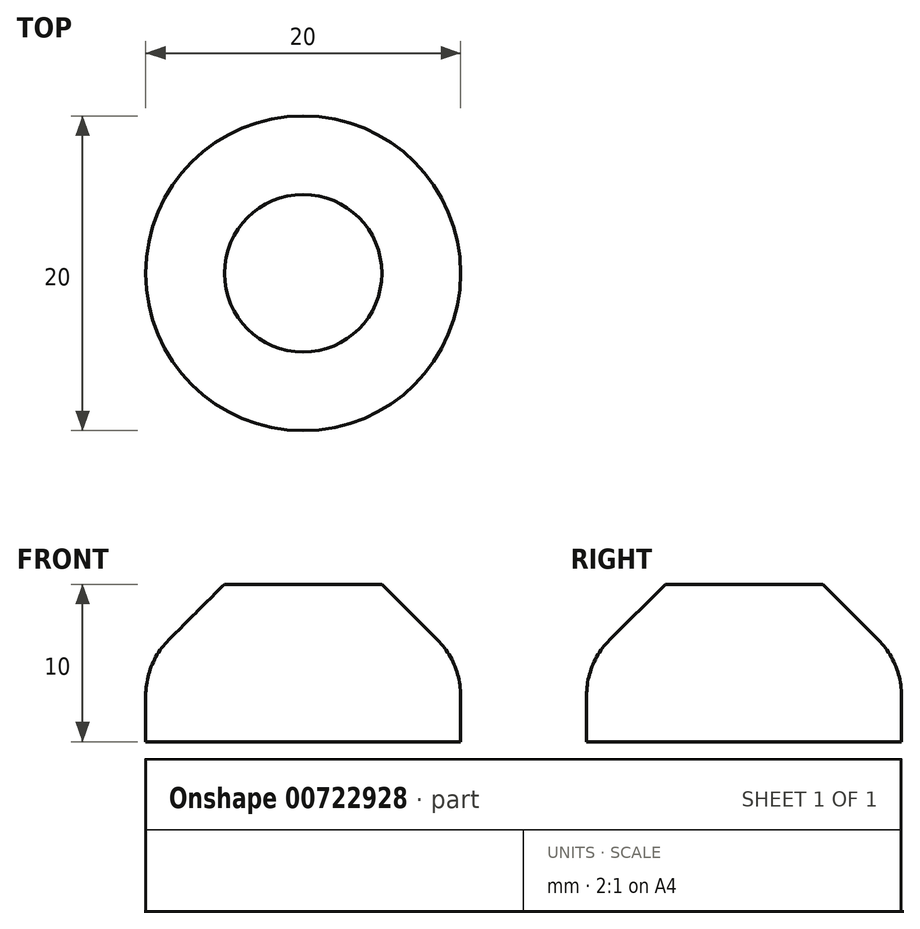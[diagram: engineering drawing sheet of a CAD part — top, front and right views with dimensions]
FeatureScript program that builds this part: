
annotation { "Feature Type Name" : "Feature", "Feature Type Description" : "" }
export const myFeature = defineFeature(function(context is Context, id is Id, definition is map)
    precondition{}
    {
        {
            var Q0;
            Q0=qCreatedBy(makeId("Top.planeOp"),FACE);
            var sketch = newSketch(context, id + "F0", { "sketchPlane" : qUnion([Q0])});
            skCircle(sketch, "E0", {"center": v(0, 0) * mm, "radius": 10 * mm});
            skSolve(sketch);
        }
        {
            var Q0;
            Q0=makeQuery(id+"F0.imprint","IMPRINT",FACE,{"disambiguationData":[TD([[makeQuery(id+"F0.imprint","IMPRINT",EDGE,{"derivedFrom":sQuery(id+"F0.wireOp",EDGE,"E0")}),1.0]])]});
            extrude(context, id + "F1", {"entities" : qUnion([Q0]), "depth" : 10 * mm, "offsetDistance" : 25 * mm});
        }
        {
            var Q0;
            Q0=makeQuery(id+"F1.opExtrude","CAP_FACE",FACE,{"disambiguationData":[OSD([sQuery(id+"F0.wireOp",EDGE,"E0")])],"isStart":false});
            chamfer(context, id + "F2", {"entities" : qUnion([Q0]), "width" : 5 * mm, "tangentPropagation" : true});
        }
        {
            var Q0;
            {var subQ0=sQuery(id+"F0.wireOp",EDGE,"E0");Q0=makeQuery(id+"F2.opChamfer","BLEND_EDGE",EDGE,{"blendedFrom":[makeQuery(id+"F1.opExtrude","CAP_EDGE",EDGE,{"disambiguationData":[OSD([subQ0])],"isStart":false}),makeQuery(id+"F1.opExtrude","SWEPT_FACE",FACE,{"disambiguationData":[OSD([subQ0])]})],"blendedInto":[makeQuery(id+"F1.opExtrude","SWEPT_FACE",FACE,{"disambiguationData":[OSD([subQ0])]})]});}
            fillet(context, id + "F3", {"entities" : qUnion([Q0]), "radius" : 5 * mm, "tangentPropagation" : true, "allowEdgeOverflow" : false});
        }
    });
